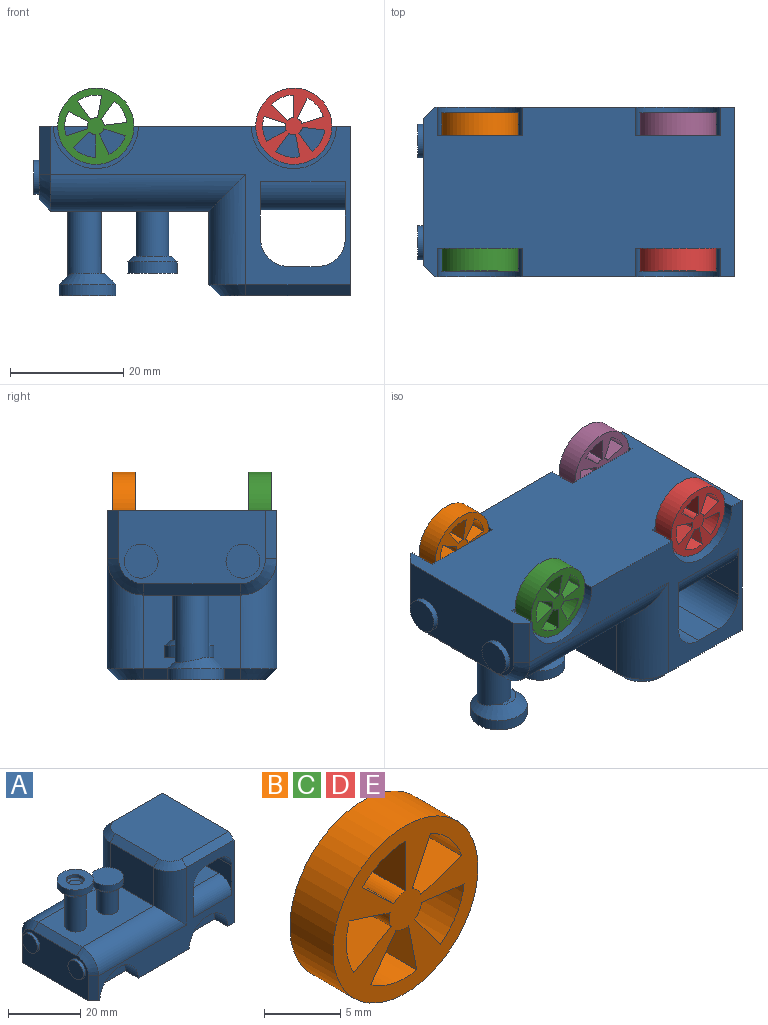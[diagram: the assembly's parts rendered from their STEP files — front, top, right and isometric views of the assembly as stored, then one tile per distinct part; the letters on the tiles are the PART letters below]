
ASSEMBLY  parts=5 mates=4
PART A: 104 faces, bbox 56x30x30 mm
  f0: cylinder r=3mm len=11.87mm, axis (0,0,-1), area 213.1mm2, adj f7,f44,f46
  f1: plane 53x28mm, normal (0,1,0), area 420.3mm2, adj f2,f5,f13,f15,f17,f18,f25,f30
  f2: plane 55x30mm, normal (0,0,-1), area 1346mm2, adj f1,f3,f5,f6,f9,f10,f11,f12
  f3: plane 53x28mm, normal (0,-1,0), area 420.3mm2, adj f2,f5,f9,f11,f19,f20,f21,f26
  f4: plane 26x23mm, normal (0,0,1), area 589.3mm2, adj f5,f26,f27,f28,f29,f30
  f5: plane 30x30mm, normal (1,0,0), area 896mm2, adj f1,f2,f3,f4,f26,f30
  f6: plane 26x13mm, normal (-1,0,0), area 272.8mm2, adj f2,f21,f22,f23,f24,f25,f39,f41
  f7: plane 28x17mm, normal (0,0,1), area 420.8mm2, adj f0,f8,f18,f19,f23,f99
  f8: plane 17x13mm, normal (-1,0,0), area 221mm2, adj f7,f17,f20,f28
  f9: cylinder r=7.5mm len=15mm, axis (0,-1,0), area 117.8mm2, adj f2,f3,f10
  f10: plane 15x7.5mm, normal (0,-1,0), area 88.4mm2, adj f2,f9
  f11: cylinder r=7.5mm len=15mm, axis (0,-1,0), area 117.8mm2, adj f2,f3,f12
  f12: plane 15x7.5mm, normal (0,-1,0), area 88.4mm2, adj f2,f11
  f13: cylinder r=7.5mm len=15mm, axis (0,1,0), area 117.8mm2, adj f1,f2,f14
  f14: plane 15x7.5mm, normal (0,1,0), area 88.4mm2, adj f2,f13
  f15: cylinder r=7.5mm len=15mm, axis (0,1,0), area 117.8mm2, adj f1,f2,f16
  f16: plane 15x7.5mm, normal (0,1,0), area 88.4mm2, adj f2,f15
  f17: cylinder r=6.5mm len=19.5mm, axis (0,0,1), area 156.8mm2, adj f1,f8,f18,f29
  f18: cylinder r=6.5mm len=34.5mm, axis (1,0,0), area 310mm2, adj f1,f7,f17,f24
  f19: cylinder r=6.5mm len=34.5mm, axis (-1,0,0), area 310mm2, adj f3,f7,f20,f22
  f20: cylinder r=6.5mm len=19.5mm, axis (0,0,-1), area 156.8mm2, adj f3,f8,f19,f27
  f21: plane 8.5x2mm, normal (-0.71,-0.71,0), area 24mm2, adj f2,f3,f6,f22
  f22: cone r=4.5mm half-angle=45deg, axis (1,0,0), area 24.4mm2, adj f6,f19,f21,f23
  f23: plane 17x2mm, normal (-0.71,0,0.71), area 48.1mm2, adj f6,f7,f22,f24
  f24: cone r=4.5mm half-angle=45deg, axis (1,0,0), area 24.4mm2, adj f6,f18,f23,f25
  f25: plane 8.5x2mm, normal (-0.71,0.71,0), area 24mm2, adj f1,f2,f6,f24
  f26: plane 18.5x2mm, normal (0,-0.71,0.71), area 52.3mm2, adj f3,f4,f5,f27
  f27: cone r=4.5mm half-angle=45deg, axis (0,0,-1), area 24.4mm2, adj f4,f20,f26,f28
  f28: plane 17x2mm, normal (-0.71,0,0.71), area 48.1mm2, adj f4,f8,f27,f29
  f29: cone r=4.5mm half-angle=45deg, axis (0,0,-1), area 24.4mm2, adj f4,f17,f28,f30
  f30: plane 18.5x2mm, normal (0,0.71,0.71), area 52.3mm2, adj f1,f4,f5,f29
  f31: plane 30x10mm, normal (-1,0,0), area 160.7mm2, adj f1,f3,f34,f35,f36,f38
  f32: plane 30x5mm, normal (0,0,-1), area 150mm2, adj f1,f3,f36,f37
  f33: plane 30x10mm, normal (1,0,0), area 160.7mm2, adj f1,f3,f34,f35,f37,f38
  f34: plane 20x15mm, normal (0,0,1), area 300mm2, adj f31,f33,f35,f38
  f35: cylinder r=5mm len=15mm, axis (1,0,0), area 117.8mm2, adj f1,f31,f33,f34
  f36: cylinder r=5mm len=30mm, axis (0,1,0), area 235.6mm2, adj f1,f3,f31,f32
  f37: cylinder r=5mm len=30mm, axis (0,-1,0), area 235.6mm2, adj f1,f3,f32,f33
  f38: cylinder r=5mm len=15mm, axis (-1,0,0), area 117.8mm2, adj f3,f31,f33,f34
  f39: cylinder r=3mm len=6mm, axis (1,0,0), area 18.8mm2, adj f6,f40
  f40: plane 6x6mm, normal (-1,0,0), area 28.3mm2, adj f39
  f41: cylinder r=3mm len=6mm, axis (1,0,0), area 18.8mm2, adj f6,f42
  f42: plane 6x6mm, normal (-1,0,0), area 28.3mm2, adj f41
  f43: cylinder r=5mm len=10mm, axis (0,0,1), area 62.8mm2, adj f45,f46
  f44: plane 5.63x5.14mm, normal (0,0,-1), area 5.2mm2, adj f0,f46
  f45: plane 10x10mm, normal (0,0,1), area 58.9mm2, adj f43,f96
  f46: cone r=5mm half-angle=45deg, axis (0,0,1), area 63.7mm2, adj f0,f43,f44
  f47: cylinder r=10mm len=17.18mm, axis (0,1,0), area 106.4mm2, adj f55,f59,f60,f64,f72,f74,f81
  f48: cylinder r=10mm len=17.18mm, axis (0,-1,0), area 106.4mm2, adj f53,f60,f61,f64,f69,f75,f77
  f49: plane 24.33x5mm, normal (0,0,1), area 121.7mm2, adj f50,f85,f89,f90
  f50: plane 16x0.54mm, normal (0,0.71,-0.71), area 8.4mm2, adj f49,f52,f53,f62,f63,f82,f89,f90
  f51: plane 25x9.8mm, normal (-1,0,0), area 201.1mm2, adj f54,f56,f60,f67,f68,f70,f71,f87
  f52: plane 1.18x0.48mm, normal (0,1,0), area 0.3mm2, adj f50,f63,f89
  f53: plane 27.74x24.46mm, normal (0,1,0), area 131mm2, adj f48,f50,f60,f67,f75,f76,f86,f90
  f54: plane 5.5x3.18mm, normal (0,1,0), area 6.6mm2, adj f51,f67,f91
  f55: plane 27.74x24.46mm, normal (0,-1,0), area 131mm2, adj f47,f60,f70,f73,f74,f85,f86,f88
  f56: plane 5.5x3.18mm, normal (0,-1,0), area 6.6mm2, adj f51,f70,f88
  f57: plane 1.18x0.48mm, normal (0,-1,0), area 0.3mm2, adj f63,f85,f89
  f58: cylinder r=0.5mm len=16mm, axis (0,0,-1), area 50.3mm2, adj f65,f97
  f59: plane 1.7x1.32mm, normal (0,-1,0), area 1mm2, adj f47,f74,f81
  f60: plane 50x25mm, normal (0,0,1), area 906.4mm2, adj f47,f48,f51,f53,f55,f64,f67,f68
  f61: plane 1.7x1.32mm, normal (0,1,0), area 1mm2, adj f48,f75,f77
  f62: plane 23.93x19.46mm, normal (0,0,-1), area 460.6mm2, adj f50,f63,f82,f83,f84,f85
  f63: plane 25x1.01mm, normal (-1,0,0), area 25mm2, adj f50,f52,f57,f62,f85,f89
  f64: plane 23.93x9.46mm, normal (1,0,0), area 183mm2, adj f47,f48,f60,f69,f72,f77,f78,f79
  f65: plane 29.46x17mm, normal (0,0,-1), area 500.1mm2, adj f58,f66,f74,f75,f79
  f66: plane 17x14.46mm, normal (1,0,0), area 245.9mm2, adj f65,f73,f76,f83
  f67: cylinder r=10mm len=17.18mm, axis (0,-1,0), area 108.3mm2, adj f51,f53,f54,f60,f68,f91
  f68: plane 17.18x7.5mm, normal (0,1,0), area 102.3mm2, adj f51,f60,f67
  f69: plane 17.18x7.5mm, normal (0,1,0), area 102.3mm2, adj f48,f60,f64
  f70: cylinder r=10mm len=17.18mm, axis (0,1,0), area 108.3mm2, adj f51,f55,f56,f60,f71,f88
  f71: plane 17.18x7.5mm, normal (0,-1,0), area 102.3mm2, adj f51,f60,f70
  f72: plane 17.18x7.5mm, normal (0,-1,0), area 102.3mm2, adj f47,f60,f64
  f73: cylinder r=4mm len=18.46mm, axis (0,0,1), area 100mm2, adj f55,f66,f74,f84
  f74: cylinder r=4mm len=33.46mm, axis (1,0,0), area 183.4mm2, adj f47,f55,f59,f65,f73,f80
  f75: cylinder r=4mm len=33.46mm, axis (-1,0,0), area 183.4mm2, adj f48,f53,f61,f65,f76,f78
  f76: cylinder r=4mm len=18.46mm, axis (0,0,-1), area 100mm2, adj f53,f66,f75,f82
  f77: plane 1.9x0.55mm, normal (0.71,0.71,0), area 1.2mm2, adj f48,f61,f64,f78
  f78: cone r=2.73mm half-angle=45deg, axis (1,0,0), area 4.4mm2, adj f64,f75,f77,f79
  f79: plane 17x0.54mm, normal (0.71,0,-0.71), area 12.9mm2, adj f64,f65,f78,f80
  f80: cone r=2.73mm half-angle=45deg, axis (1,0,0), area 4.4mm2, adj f64,f74,f79,f81
  f81: plane 1.9x0.55mm, normal (0.71,-0.71,0), area 1.2mm2, adj f47,f59,f64,f80
  f82: cone r=2.73mm half-angle=45deg, axis (0,0,-1), area 4.4mm2, adj f50,f62,f76,f83
  f83: plane 17x0.54mm, normal (0.71,0,-0.71), area 12.9mm2, adj f62,f66,f82,f84
  f84: cone r=2.73mm half-angle=45deg, axis (0,0,-1), area 4.4mm2, adj f62,f73,f83,f85
  f85: plane 16x0.54mm, normal (0,-0.71,-0.71), area 8.4mm2, adj f49,f55,f57,f62,f63,f84,f89,f90
  f86: plane 25x10mm, normal (-1,0,0), area 190.2mm2, adj f53,f55,f87,f88,f90,f91
  f87: plane 20x15.89mm, normal (0,0,-1), area 317.8mm2, adj f51,f86,f88,f91
  f88: cylinder r=2.5mm len=15.89mm, axis (1,0,0), area 61.9mm2, adj f51,f55,f56,f70,f86,f87
  f89: cylinder r=7.5mm len=25mm, axis (0,1,0), area 87mm2, adj f49,f50,f52,f57,f63,f85
  f90: cylinder r=7.5mm len=25mm, axis (0,-1,0), area 293.5mm2, adj f49,f50,f53,f55,f85,f86
  f91: cylinder r=2.5mm len=15.89mm, axis (-1,0,0), area 61.9mm2, adj f51,f53,f54,f67,f86,f87
  f92: cylinder r=0.5mm len=1mm, axis (1,0,0), area 3.1mm2, adj f64,f93
  f93: plane 1x1mm, normal (1,0,0), area 0.8mm2, adj f92
  f94: cylinder r=0.5mm len=1mm, axis (1,0,0), area 3.1mm2, adj f64,f95
  f95: plane 1x1mm, normal (1,0,0), area 0.8mm2, adj f94
  f96: cylinder r=2.5mm len=5mm, axis (0,0,1), area 15.1mm2, adj f45,f98
  f97: plane 3.93x3.93mm, normal (0,0,1), area 11.3mm2, adj f58,f98
  f98: cone r=3.23mm half-angle=45deg, axis (0,0,1), area 10.6mm2, adj f96,f97
  f99: cylinder r=2.93mm len=8mm, axis (0,0,-1), area 147.2mm2, adj f7,f102
  f100: cylinder r=4.38mm len=8.76mm, axis (0,0,-1), area 55mm2, adj f101,f103
  f101: plane 8.76x8.76mm, normal (0,0,1), area 60.2mm2, adj f100
  f102: plane 6.76x6.76mm, normal (0,0,-1), area 8.9mm2, adj f99,f103
  f103: cone r=4.38mm half-angle=45deg, axis (0,0,1), area 34.5mm2, adj f100,f102
PART B: 23 faces, bbox 13.5x4x13.5 mm
  f0: cylinder r=6.75mm len=13.5mm, axis (0,1,0), area 169.6mm2, adj f1,f2
  f1: plane 13.5x13.5mm, normal (0,-1,0), area 85.7mm2, adj f0,f3,f4,f5,f6,f7,f8,f9
  f2: plane 13.5x13.5mm, normal (0,1,0), area 85.7mm2, adj f0,f3,f4,f5,f6,f7,f8,f9
  f3: cylinder r=5.5mm len=4.02mm, axis (0,-1,0), area 18mm2, adj f1,f2,f4,f6
  f4: plane 4x2.93mm, normal (0.68,0,0.73), area 16mm2, adj f1,f2,f3,f5
  f5: cylinder r=1.5mm len=4mm, axis (0,-1,0), area 4.9mm2, adj f1,f2,f4,f6
  f6: plane 4x4mm, normal (-1,0,0), area 16mm2, adj f1,f2,f3,f5
  f7: cylinder r=5.5mm len=4.28mm, axis (0,-1,0), area 18mm2, adj f1,f2,f8,f10
  f8: plane 4x3.93mm, normal (-0.98,0,-0.19), area 16mm2, adj f1,f2,f7,f9
  f9: cylinder r=1.5mm len=4mm, axis (0,-1,0), area 4.9mm2, adj f1,f2,f8,f10
  f10: plane 4x3.24mm, normal (0.81,0,-0.59), area 16mm2, adj f1,f2,f7,f9
  f11: cylinder r=5.5mm len=4.37mm, axis (0,-1,0), area 18mm2, adj f1,f2,f12,f14
  f12: plane 4x3.5mm, normal (-0.48,0,0.87), area 16mm2, adj f1,f2,f11,f13
  f13: cylinder r=1.5mm len=4mm, axis (0,-1,0), area 4.9mm2, adj f1,f2,f12,f14
  f14: plane 4x3.8mm, normal (-0.31,0,-0.95), area 16mm2, adj f1,f2,f11,f13
  f15: cylinder r=5.5mm len=4mm, axis (0,-1,0), area 18mm2, adj f1,f2,f16,f18
  f16: plane 4x3.97mm, normal (-0.12,0,-0.99), area 16mm2, adj f1,f2,f15,f17
  f17: cylinder r=1.5mm len=4mm, axis (0,-1,0), area 4.9mm2, adj f1,f2,f16,f18
  f18: plane 4x3.24mm, normal (0.81,0,0.59), area 16mm2, adj f1,f2,f15,f17
  f19: cylinder r=5.5mm len=4mm, axis (0,-1,0), area 18mm2, adj f1,f2,f20,f22
  f20: plane 4x3.63mm, normal (0.91,0,-0.42), area 16mm2, adj f1,f2,f19,f21
  f21: cylinder r=1.5mm len=4mm, axis (0,-1,0), area 4.9mm2, adj f1,f2,f20,f22
  f22: plane 4x3.8mm, normal (-0.31,0,0.95), area 16mm2, adj f1,f2,f19,f21
PART C: same geometry as B
PART D: same geometry as B
PART E: same geometry as B
PLACE A rot(axis=(1,0,0),180deg) t=(-5.84,10.21,8.5)mm
PLACE B rot(axis=(1,0,0),180deg) t=(-23.34,20.21,8.5)mm
PLACE C rot(axis=(1,0,0),180deg) t=(-23.34,-3.79,8.5)mm
PLACE D t=(11.66,0.21,8.5)mm
PLACE E t=(11.66,24.21,8.5)mm
MATE fastened C.f0 <-> A.f15  axis (0,1,0) through (-23.34,0.21,8.5)mm
MATE fastened A.f13 <-> D.f0  axis (0,-1,0) through (11.66,0.21,8.5)mm
MATE fastened A.f9 <-> E.f0  axis (0,1,0) through (11.66,20.21,8.5)mm
MATE fastened A.f11 <-> B.f0  axis (0,1,0) through (-23.34,20.21,8.5)mm
